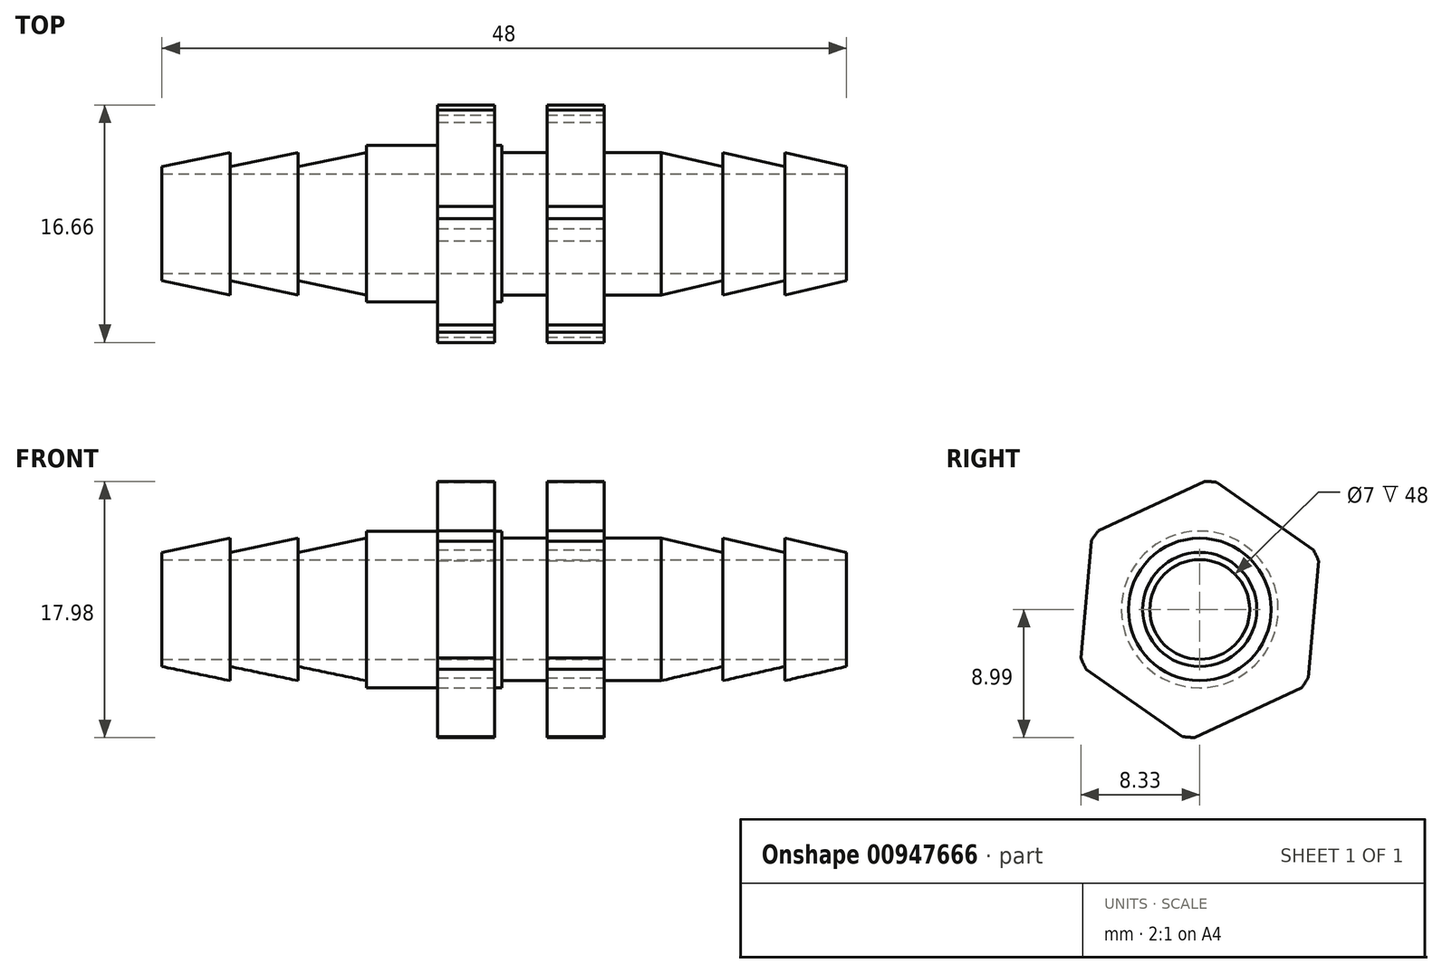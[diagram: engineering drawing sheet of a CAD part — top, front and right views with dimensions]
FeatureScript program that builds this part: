
annotation { "Feature Type Name" : "Feature", "Feature Type Description" : "" }
export const myFeature = defineFeature(function(context is Context, id is Id, definition is map)
    precondition{}
    {
        {
            var Q0;
            Q0=qCreatedBy(makeId("Front.planeOp"),FACE);
            var sketch = newSketch(context, id + "F0", { "sketchPlane" : qUnion([Q0])});
            skLineSegment(sketch, "E0", {"start": v(0, 0) * mm, "end": v(-48, 0) * mm});
            skLineSegment(sketch, "E1", {"start": v(-48, 3.5) * mm, "end": v(-48, 4) * mm});
            skLineSegment(sketch, "E2", {"start": v(-17, 5) * mm, "end": v(-17, 9) * mm});
            skLineSegment(sketch, "E3", {"start": v(-17, 9) * mm, "end": v(-21, 9) * mm});
            skLineSegment(sketch, "E4", {"start": v(-17, 5) * mm, "end": v(-13, 5) * mm});
            skLineSegment(sketch, "E5", {"start": v(0, 3.5) * mm, "end": v(0, 4) * mm});
            skLineSegment(sketch, "E6", {"start": v(0, 4) * mm, "end": v(-4.33, 5) * mm});
            skLineSegment(sketch, "E7", {"start": v(-4.33, 5) * mm, "end": v(-4.33, 4) * mm});
            skLineSegment(sketch, "E8", {"start": v(-4.33, 4) * mm, "end": v(-8.67, 5) * mm});
            skLineSegment(sketch, "E9", {"start": v(-8.67, 5) * mm, "end": v(-8.67, 4) * mm});
            skLineSegment(sketch, "E10", {"start": v(-8.67, 4) * mm, "end": v(-13, 5) * mm});
            skLineSegment(sketch, "E11", {"start": v(-21, 9) * mm, "end": v(-21, 5) * mm});
            skLineSegment(sketch, "E12", {"start": v(-21, 5) * mm, "end": v(-24.18, 5) * mm});
            skLineSegment(sketch, "E13", {"start": v(-24.18, 5) * mm, "end": v(-24.18, 5.5) * mm});
            skLineSegment(sketch, "E14", {"start": v(-24.18, 5.5) * mm, "end": v(-24.68, 5.5) * mm});
            skLineSegment(sketch, "E15", {"start": v(-24.68, 5.5) * mm, "end": v(-24.68, 9) * mm});
            skLineSegment(sketch, "E16", {"start": v(-24.68, 9) * mm, "end": v(-28.68, 9) * mm});
            skLineSegment(sketch, "E17", {"start": v(-28.68, 9) * mm, "end": v(-28.68, 5.5) * mm});
            skLineSegment(sketch, "E18", {"start": v(-28.68, 5.5) * mm, "end": v(-33.68, 5.5) * mm});
            skLineSegment(sketch, "E19", {"start": v(-33.68, 5.5) * mm, "end": v(-33.68, 5) * mm});
            skLineSegment(sketch, "E20", {"start": v(-33.67, 5) * mm, "end": v(-38.45, 4) * mm});
            skLineSegment(sketch, "E21", {"start": v(-38.45, 4) * mm, "end": v(-38.45, 5) * mm});
            skLineSegment(sketch, "E22", {"start": v(-38.45, 5) * mm, "end": v(-43.23, 4) * mm});
            skLineSegment(sketch, "E23", {"start": v(-43.23, 4) * mm, "end": v(-43.23, 5) * mm});
            skLineSegment(sketch, "E24", {"start": v(-43.23, 5) * mm, "end": v(-48, 4) * mm});
            skPoint(sketch, "E25.orphan", {"position": v(-48, 5) * mm});
            skLineSegment(sketch, "E26", {"start": v(-48, 3.5) * mm, "end": v(0, 3.5) * mm});
            skPoint(sketch, "E26.endSnap0", {"position": v(0, 2) * mm});
            skSolve(sketch);
        }
        {
            var Q0;
            Q0 = qSketchRegion(id + "F0", true);
            var Q1;
            Q1=sQuery(id+"F0.wireOp",EDGE,"E0");
            revolve(context, id + "F1", {"surfaceOperationType" : NewSurfaceOperationType.NEW, "entities" : qUnion([Q0]), "axis" : qUnion([Q1]), "revolveType" : RevolveType.FULL});
        }
        {
            var Q0;
            Q0=qCreatedBy(makeId("Right.planeOp"),FACE);
            var sketch = newSketch(context, id + "F2", { "sketchPlane" : qUnion([Q0])});
            skCircle(sketch, "E27.cCircle", {"center": v(0, 0) * mm, "radius": 8 * mm, "construction": true});
            skLineSegment(sketch, "E27.0", {"start": v(8.37, 3.9) * mm, "end": v(7.57, -5.3) * mm});
            skLineSegment(sketch, "E27.1", {"start": v(7.57, -5.3) * mm, "end": v(-0.8, -9.2) * mm});
            skLineSegment(sketch, "E27.2", {"start": v(-0.8, -9.2) * mm, "end": v(-8.37, -3.9) * mm});
            skLineSegment(sketch, "E27.3", {"start": v(-8.37, -3.9) * mm, "end": v(-7.57, 5.3) * mm});
            skLineSegment(sketch, "E27.4", {"start": v(-7.57, 5.3) * mm, "end": v(0.8, 9.2) * mm});
            skLineSegment(sketch, "E27.5", {"start": v(0.8, 9.2) * mm, "end": v(8.37, 3.9) * mm});
            skPoint(sketch, "E27.0.midPoint", {"position": v(7.97, -0.7) * mm});
            skCircle(sketch, "E28", {"center": v(0, 0) * mm, "radius": 19 * mm});
            skSolve(sketch);
        }
        {
            var Q0;
            Q0 = qSketchRegion(id + "F2", true);
            extrude(context, id + "F3", {"entities" : qUnion([Q0]), "operationType" : NewBodyOperationType.REMOVE, "oppositeDirection" : true, "depth" : 50.9 * mm, "offsetDistance" : 25 * mm});
        }
    });
